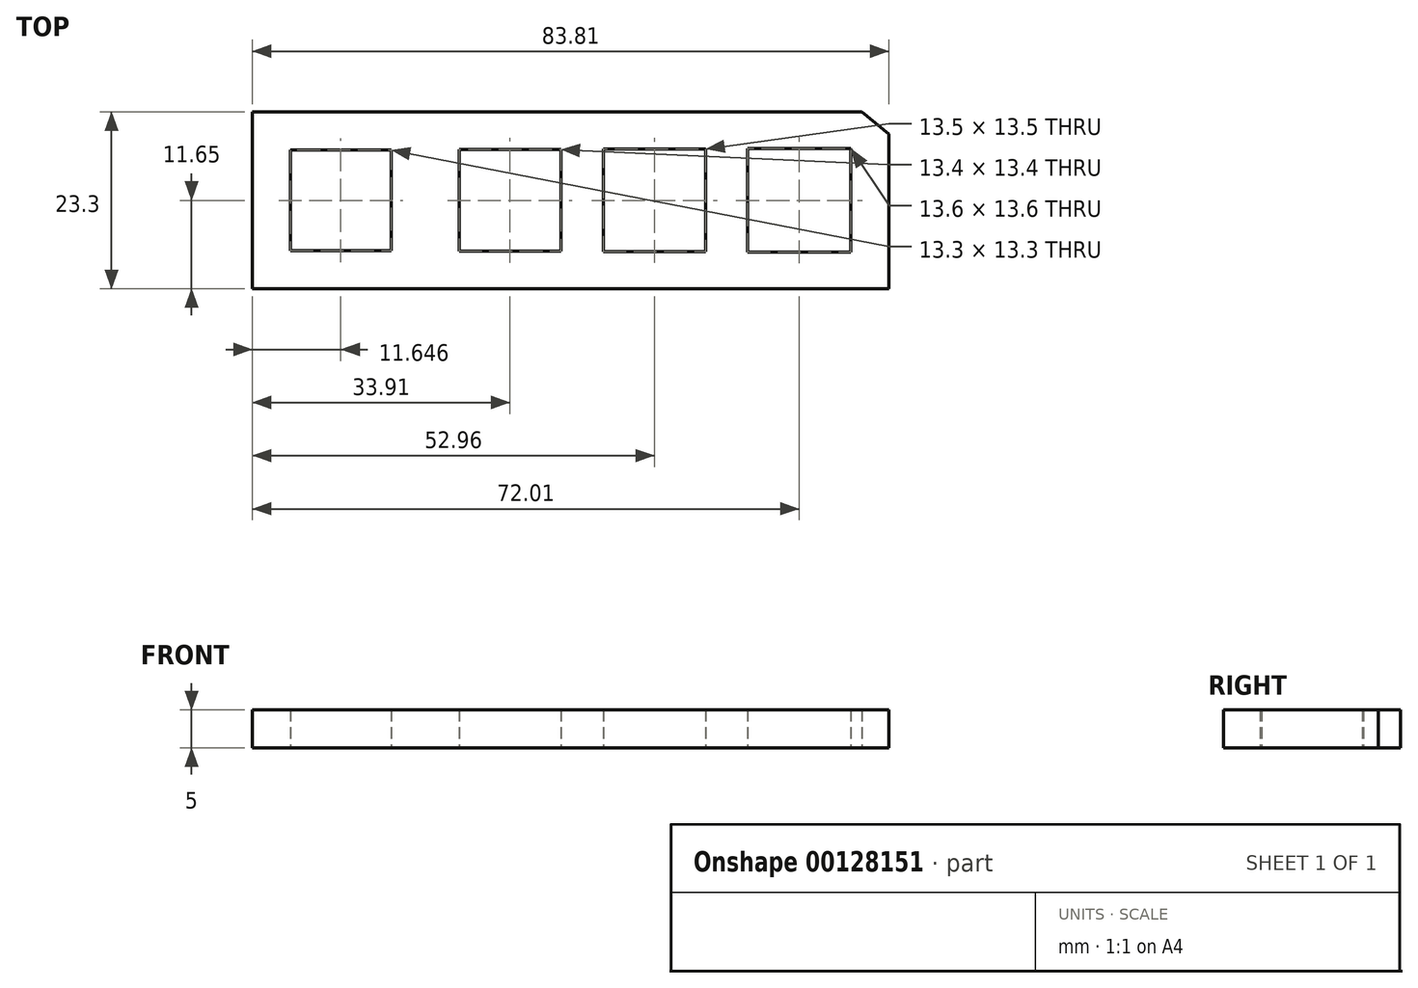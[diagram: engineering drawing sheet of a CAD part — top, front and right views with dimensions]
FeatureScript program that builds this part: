
annotation { "Feature Type Name" : "Feature", "Feature Type Description" : "" }
export const myFeature = defineFeature(function(context is Context, id is Id, definition is map)
    precondition{}
    {
        {
            var Q0;
            Q0=qCreatedBy(makeId("Top.planeOp"),FACE);
            var sketch = newSketch(context, id + "F0", { "sketchPlane" : qUnion([Q0])});
            skLineSegment(sketch, "E0.bottom", {"start": v(-6.75, 6.75) * mm, "end": v(6.75, 6.75) * mm});
            skLineSegment(sketch, "E0.top", {"start": v(-6.75, -6.75) * mm, "end": v(6.75, -6.75) * mm});
            skLineSegment(sketch, "E0.left", {"start": v(-6.75, 6.75) * mm, "end": v(-6.75, -6.75) * mm});
            skLineSegment(sketch, "E0.right", {"start": v(6.75, 6.75) * mm, "end": v(6.75, -6.75) * mm});
            skPoint(sketch, "E0.middle", {"position": v(0, 0) * mm});
            skLineSegment(sketch, "E1.bottom", {"start": v(-12.35, -6.7) * mm, "end": v(-25.75, -6.7) * mm});
            skLineSegment(sketch, "E1.top", {"start": v(-12.35, 6.7) * mm, "end": v(-25.75, 6.7) * mm});
            skLineSegment(sketch, "E1.left", {"start": v(-12.35, -6.7) * mm, "end": v(-12.35, 6.7) * mm});
            skLineSegment(sketch, "E1.right", {"start": v(-25.75, -6.7) * mm, "end": v(-25.75, 6.7) * mm});
            skPoint(sketch, "E1.middle", {"position": v(-19.05, 0) * mm});
            skLineSegment(sketch, "E2.bottom", {"start": v(25.85, -6.8) * mm, "end": v(12.25, -6.8) * mm});
            skLineSegment(sketch, "E2.top", {"start": v(25.85, 6.8) * mm, "end": v(12.25, 6.8) * mm});
            skLineSegment(sketch, "E2.left", {"start": v(25.85, -6.8) * mm, "end": v(25.85, 6.8) * mm});
            skLineSegment(sketch, "E2.right", {"start": v(12.25, -6.8) * mm, "end": v(12.25, 6.8) * mm});
            skPoint(sketch, "E2.middle", {"position": v(19.05, 0) * mm});
            skLineSegment(sketch, "E3.bottom", {"start": v(-34.66, -6.65) * mm, "end": v(-47.96, -6.65) * mm});
            skLineSegment(sketch, "E3.top", {"start": v(-34.66, 6.65) * mm, "end": v(-47.96, 6.65) * mm});
            skLineSegment(sketch, "E3.left", {"start": v(-34.66, -6.65) * mm, "end": v(-34.66, 6.65) * mm});
            skLineSegment(sketch, "E3.right", {"start": v(-47.96, -6.65) * mm, "end": v(-47.96, 6.65) * mm});
            skPoint(sketch, "E3.middle", {"position": v(-41.31, 0) * mm});
            skLineSegment(sketch, "E4.bottom", {"start": v(-52.96, 11.65) * mm, "end": v(27.3, 11.65) * mm});
            skLineSegment(sketch, "E4.top", {"start": v(-52.96, -11.65) * mm, "end": v(30.85, -11.65) * mm});
            skLineSegment(sketch, "E4.left", {"start": v(-52.96, 11.65) * mm, "end": v(-52.96, -11.65) * mm});
            skLineSegment(sketch, "E4.right", {"start": v(30.85, 8.72) * mm, "end": v(30.85, -11.65) * mm});
            skLineSegment(sketch, "E5", {"start": v(27.3, 11.65) * mm, "end": v(30.85, 8.72) * mm});
            skSolve(sketch);
        }
        {
            var Q0;
            Q0 = qSketchRegion(id + "F0", true);
            extrude(context, id + "F1", {"entities" : qUnion([Q0]), "depth" : 5 * mm});
        }
    });
